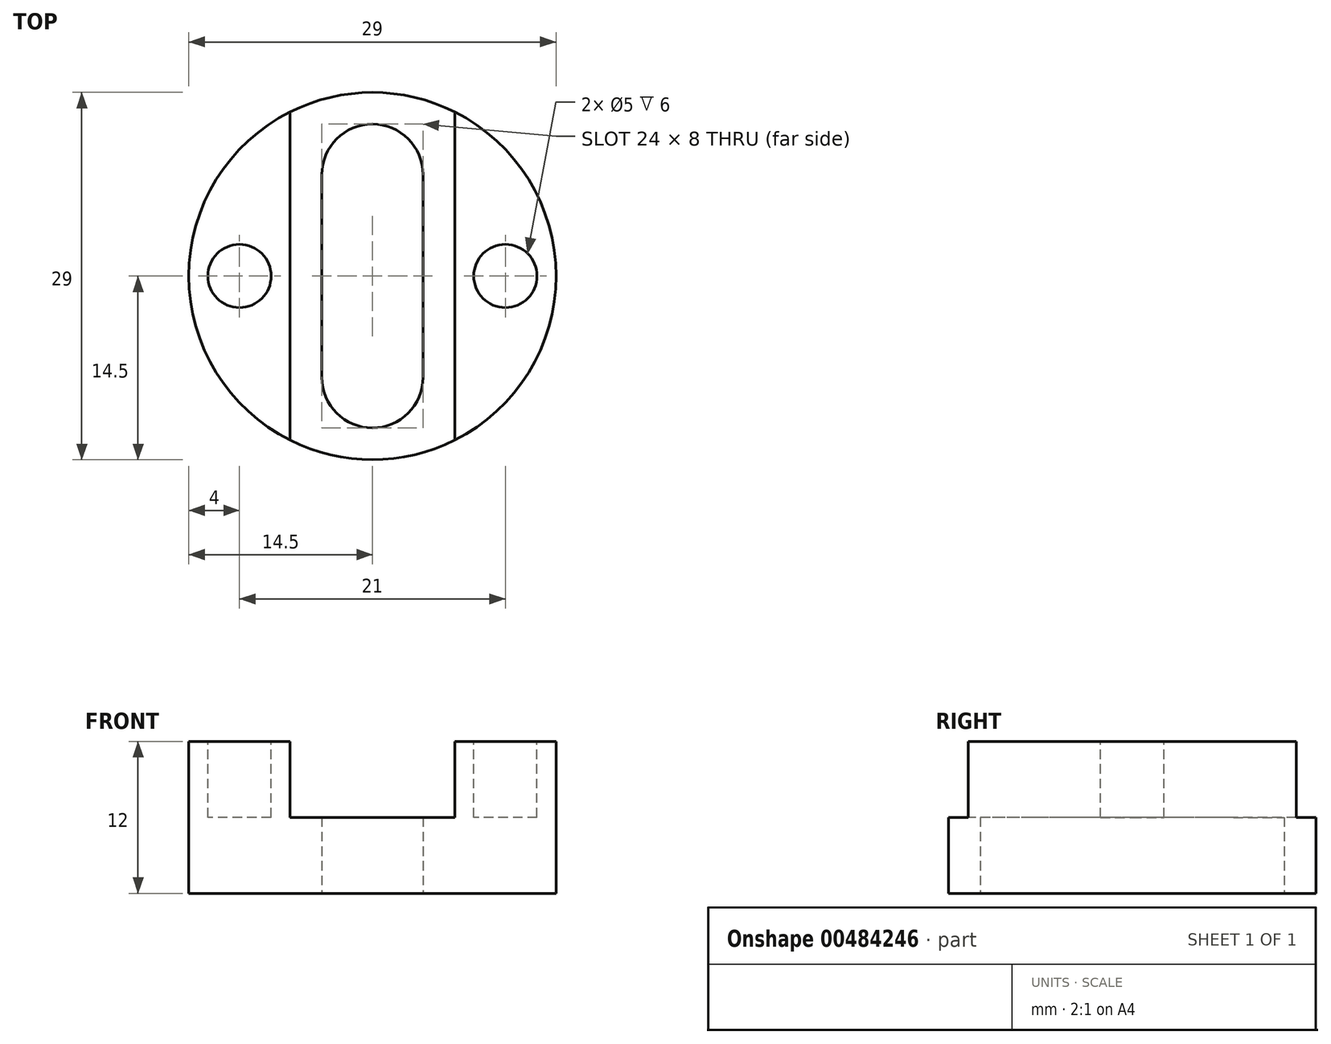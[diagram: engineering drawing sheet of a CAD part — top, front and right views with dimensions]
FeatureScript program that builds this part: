
annotation { "Feature Type Name" : "Feature", "Feature Type Description" : "" }
export const myFeature = defineFeature(function(context is Context, id is Id, definition is map)
    precondition{}
    {
        {
            var Q0;
            Q0=qCreatedBy(makeId("Top.planeOp"),FACE);
            var sketch = newSketch(context, id + "F0", { "sketchPlane" : qUnion([Q0])});
            skCircle(sketch, "E0", {"center": v(0, 0) * mm, "radius": 14.5 * mm});
            skLineSegment(sketch, "E1", {"start": v(-4, 8) * mm, "end": v(-4, -8) * mm});
            skLineSegment(sketch, "E2", {"start": v(4, -8) * mm, "end": v(4, 8) * mm});
            skArc(sketch, "E3", {"start": v(-4, -8) * mm, "mid": v(0, -12) * mm, "end": v(4, -8) * mm});
            skArc(sketch, "E4", {"start": v(4, 8) * mm, "mid": v(0, 12) * mm, "end": v(-4, 8) * mm});
            skLineSegment(sketch, "E5", {"start": v(-4, 0) * mm, "end": v(4, 0) * mm, "construction": true});
            skSolve(sketch);
        }
        {
            var Q0;
            Q0 = qSketchRegion(id + "F0", true);
            extrude(context, id + "F1", {"entities" : qUnion([Q0]), "depth" : 12 * mm});
        }
        {
            var Q0;
            Q0=makeQuery(id+"F1.opExtrude","CAP_FACE",FACE,{"disambiguationData":[OSD([sQuery(id+"F0.wireOp",EDGE,"E0"),sQuery(id+"F0.wireOp",EDGE,"E1"),sQuery(id+"F0.wireOp",EDGE,"E2"),sQuery(id+"F0.wireOp",EDGE,"E3"),sQuery(id+"F0.wireOp",EDGE,"E4")])],"isStart":false});
            var sketch = newSketch(context, id + "F2", { "sketchPlane" : qUnion([Q0])});
            skLineSegment(sketch, "E6", {"start": v(-6.5, 12.96) * mm, "end": v(-6.5, -12.96) * mm});
            skLineSegment(sketch, "E7", {"start": v(6.5, -12.96) * mm, "end": v(6.5, 12.96) * mm});
            skCircle(sketch, "E8", {"center": v(-10.5, 0) * mm, "radius": 2.5 * mm});
            skLineSegment(sketch, "E9", {"start": v(-6.5, 0) * mm, "end": v(-14.5, 0) * mm, "construction": true});
            skLineSegment(sketch, "E10", {"start": v(0, 14.5) * mm, "end": v(0, -14.5) * mm, "construction": true});
            skPoint(sketch, "E10.endSnap0", {"position": v(0, -12) * mm});
            skLineSegment(sketch, "E11.MirrorCS", {"start": v(6.5, 0) * mm, "end": v(14.5, 0) * mm, "construction": true});
            skCircle(sketch, "E12.MirrorC", {"center": v(10.5, 0) * mm, "radius": 2.5 * mm});
            skSolve(sketch);
        }
        {
            var Q0;
            Q0 = qSketchRegion(id + "F2", true);
            var Q1;
            {var subQ1=sQuery(id+"F2.wireOp",EDGE,"E6");Q1=makeQuery(id+"F2.imprint","IMPRINT",FACE,{"disambiguationData":[TD([[makeQuery(id+"F2.imprint","IMPRINT",EDGE,{"derivedFrom":subQ1}),1.0]])]});}
            extrude(context, id + "F3", {"entities" : qUnion([Q0, Q1]), "operationType" : NewBodyOperationType.REMOVE, "oppositeDirection" : true, "depth" : 6 * mm});
        }
    });
